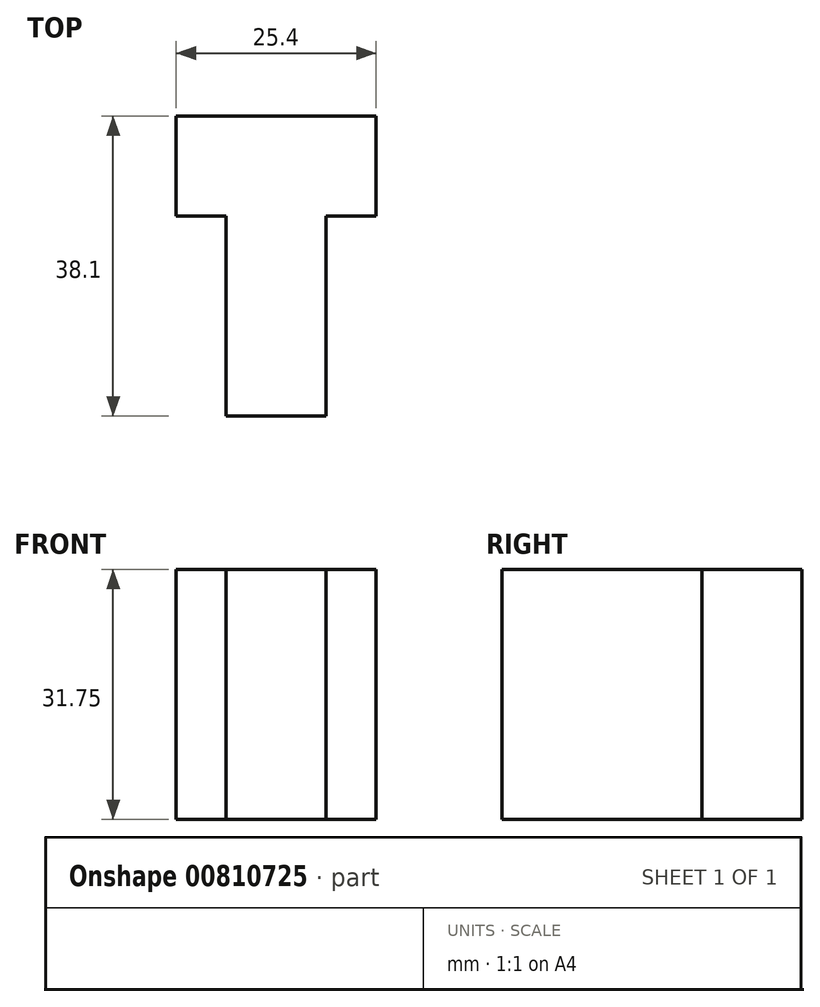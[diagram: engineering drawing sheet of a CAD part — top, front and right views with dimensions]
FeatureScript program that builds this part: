
annotation { "Feature Type Name" : "Feature", "Feature Type Description" : "" }
export const myFeature = defineFeature(function(context is Context, id is Id, definition is map)
    precondition{}
    {
        {
            var Q0;
            Q0=qCreatedBy(makeId("Top.planeOp"),FACE);
            var sketch = newSketch(context, id + "F0", { "sketchPlane" : qUnion([Q0])});
            skLineSegment(sketch, "E0", {"start": v(0, 0) * mm, "end": v(-12.7, 0) * mm});
            skLineSegment(sketch, "E1", {"start": v(-12.7, 0) * mm, "end": v(-12.7, 25.4) * mm});
            skLineSegment(sketch, "E2", {"start": v(-12.7, 25.4) * mm, "end": v(-19.05, 25.4) * mm});
            skLineSegment(sketch, "E3", {"start": v(-19.05, 25.4) * mm, "end": v(-19.05, 38.1) * mm});
            skLineSegment(sketch, "E4", {"start": v(-19.05, 38.1) * mm, "end": v(6.35, 38.1) * mm});
            skLineSegment(sketch, "E5", {"start": v(6.35, 38.1) * mm, "end": v(6.35, 25.4) * mm});
            skLineSegment(sketch, "E6", {"start": v(6.35, 25.4) * mm, "end": v(0, 25.4) * mm});
            skLineSegment(sketch, "E7", {"start": v(0, 25.4) * mm, "end": v(0, 0) * mm});
            skSolve(sketch);
        }
        {
            var Q0;
            Q0=makeQuery(id+"F0.imprint","IMPRINT",FACE,{"disambiguationData":[TD([[makeQuery(id+"F0.imprint","IMPRINT",EDGE,{"derivedFrom":sQuery(id+"F0.wireOp",EDGE,"E0")}),-1.0]])]});
            extrude(context, id + "F1", {"entities" : qUnion([Q0]), "depth" : 25.4 * mm, "offsetDistance" : 25.4 * mm});
        }
        {
            var Q0;
            Q0=makeQuery(id+"F1.opExtrude","CAP_FACE",FACE,{"disambiguationData":[OSD([sQuery(id+"F0.wireOp",EDGE,"E0"),sQuery(id+"F0.wireOp",EDGE,"E1"),sQuery(id+"F0.wireOp",EDGE,"E2"),sQuery(id+"F0.wireOp",EDGE,"E3"),sQuery(id+"F0.wireOp",EDGE,"E4"),sQuery(id+"F0.wireOp",EDGE,"E5"),sQuery(id+"F0.wireOp",EDGE,"E6"),sQuery(id+"F0.wireOp",EDGE,"E7")])],"isStart":false});
            extrude(context, id + "F2", {"entities" : qUnion([Q0]), "operationType" : NewBodyOperationType.ADD, "oppositeDirection" : true, "depth" : 31.75 * mm, "offsetDistance" : 25.4 * mm});
        }
    });
